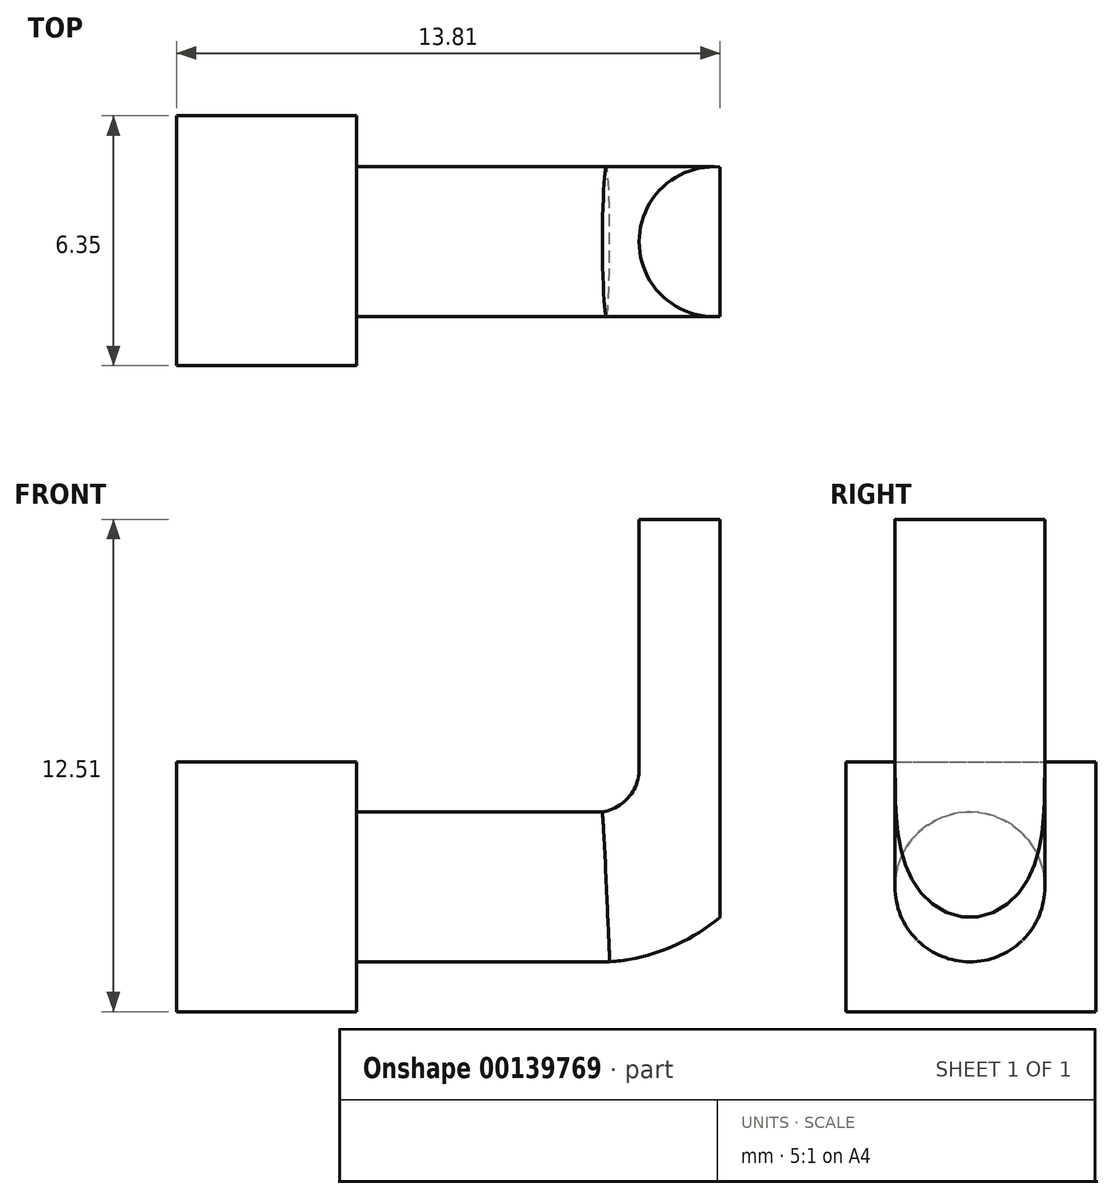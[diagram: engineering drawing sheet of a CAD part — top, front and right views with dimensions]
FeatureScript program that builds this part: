
annotation { "Feature Type Name" : "Feature", "Feature Type Description" : "" }
export const myFeature = defineFeature(function(context is Context, id is Id, definition is map)
    precondition{}
    {
        {
            var Q0;
            Q0=qCreatedBy(makeId("Front.planeOp"),FACE);
            var sketch = newSketch(context, id + "F0", { "sketchPlane" : qUnion([Q0])});
            skLineSegment(sketch, "E0", {"start": v(-11.36, 0) * mm, "end": v(-5.01, 0) * mm});
            skLineSegment(sketch, "E1", {"start": v(-2.28, 3) * mm, "end": v(-2.28, 9.34) * mm});
            skArc(sketch, "E2", {"start": v(-5.01, 0) * mm, "mid": v(-3.06, 0.96) * mm, "end": v(-2.28, 3) * mm});
            skSolve(sketch);
        }
        {
            var Q0;
            Q0=sQuery(id+"F0.wireOp",VERTEX,"E1.end");
            var Q1;
            Q1=qCreatedBy(makeId("Top.planeOp"),FACE);
            cPlane(context, id + "F1", {"entities" : qUnion([Q0, Q1]), "cplaneType" : CPlaneType.PLANE_POINT, "offset" : 25.4 * mm, "width" : 152.4 * mm, "height" : 152.4 * mm});
        }
        {
            var Q0;
            Q0=qCreatedBy(id+"F1.planeOp",FACE);
            var sketch = newSketch(context, id + "F2", { "sketchPlane" : qUnion([Q0])});
            skCircle(sketch, "E3", {"center": v(-2.28, 0.01) * mm, "radius": 1.9 * mm});
            skSolve(sketch);
        }
        {
            var Q0;
            Q0=makeQuery(id+"F2.imprint","IMPRINT",FACE,{"disambiguationData":[TD([[makeQuery(id+"F2.imprint","IMPRINT",EDGE,{"derivedFrom":sQuery(id+"F2.wireOp",EDGE,"E3")}),1.0]])]});
            var Q1;
            Q1=sQuery(id+"F0.wireOp",EDGE,"E1");
            var Q2;
            Q2=sQuery(id+"F0.wireOp",EDGE,"E2");
            var Q3;
            Q3=sQuery(id+"F0.wireOp",EDGE,"E0");
            sweep(context, id + "F3", {"profiles" : qUnion([Q0]), "path" : qUnion([Q1, Q2, Q3])});
        }
        {
            var Q0;
            Q0=makeQuery(id+"F3.opSweep","CAP_FACE",FACE,{"disambiguationData":[OSD([sQuery(id+"F0.wireOp",VERTEX,"E0.start"),sQuery(id+"F2.wireOp",EDGE,"E3")])],"isStart":false});
            var sketch = newSketch(context, id + "F4", { "sketchPlane" : qUnion([Q0])});
            skLineSegment(sketch, "E4", {"start": v(-0.04, 1.9) * mm, "end": v(-0.04, -1.9) * mm});
            skLineSegment(sketch, "E5.bottom", {"start": v(3.14, 3.18) * mm, "end": v(-3.21, 3.18) * mm});
            skLineSegment(sketch, "E5.top", {"start": v(3.14, -3.17) * mm, "end": v(-3.21, -3.17) * mm});
            skLineSegment(sketch, "E5.left", {"start": v(3.14, 3.18) * mm, "end": v(3.14, -3.17) * mm});
            skLineSegment(sketch, "E5.right", {"start": v(-3.21, 3.18) * mm, "end": v(-3.21, -3.17) * mm});
            skPoint(sketch, "E5.middle", {"position": v(-0.04, 0) * mm});
            skSolve(sketch);
        }
        {
            var Q0;
            Q0 = qSketchRegion(id + "F4", true);
            extrude(context, id + "F5", {"entities" : qUnion([Q0]), "operationType" : NewBodyOperationType.ADD, "depth" : 4.57 * mm});
        }
        {
            var Q0;
            Q0=qCreatedBy(makeId("Front.planeOp"),FACE);
            var sketch = newSketch(context, id + "F6", { "sketchPlane" : qUnion([Q0])});
            skLineSegment(sketch, "E6", {"start": v(-2.13, 10.21) * mm, "end": v(-2.13, -6.32) * mm});
            skLineSegment(sketch, "E7", {"start": v(-2.13, -6.32) * mm, "end": v(0.45, -6.32) * mm});
            skLineSegment(sketch, "E8", {"start": v(0.45, -6.32) * mm, "end": v(0.45, 10.16) * mm});
            skLineSegment(sketch, "E9", {"start": v(0.45, 10.16) * mm, "end": v(-2.13, 10.21) * mm});
            skSolve(sketch);
        }
        {
            var Q0;
            Q0 = qSketchRegion(id + "F6", true);
            extrude(context, id + "F7", {"entities" : qUnion([Q0]), "operationType" : NewBodyOperationType.REMOVE, "oppositeDirection" : true, "depth" : 25.4 * mm, "hasSecondDirection" : true, "secondDirectionOppositeDirection" : false, "secondDirectionDepth" : 25.4 * mm});
        }
    });
